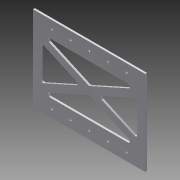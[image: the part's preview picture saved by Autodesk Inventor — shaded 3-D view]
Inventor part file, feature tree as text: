
AUTODESK INVENTOR PART (.ipt)
format: ipt  version: 2015 (Build 190159000, 159)  size: 210,944 bytes
history: native  units: in
note: dims shown in document units (in); Inventor stores cm internally (conversion verified against a paired STEP export)
features: other x6, hole x1, chamfer x1
ambient origin geometry x8: Origin, YZ Plane, XZ Plane, XY Plane, X Axis, Y Axis, Z Axis, Center Point
bodies: Solid1 (feature_tree)
feature tree (8):
  other  "profile"
  hole  "rv_holes"  [1 undecoded]
  chamfer  "Corner Round3"
  other  "profile sketch"
  other  "Plate1"
  other  "rv_hole_sketch"
  other  "cutout_sketch"
  other  "Cut2"
note: 1 required parameter value undecoded (feature->parameter linkage not recoverable at this tier; creation-order binding heuristic only, values carry confidence <= 0.55)
